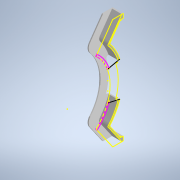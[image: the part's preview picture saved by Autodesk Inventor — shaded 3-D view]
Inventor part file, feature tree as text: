
AUTODESK INVENTOR PART (.ipt)
format: ipt  version: 2022 (Build 260153000, 153)  size: 368,128 bytes
history: native  units: mm
features: reference x28, other x7, projected_geometry x7, sketch x4, extrude x3, fillet x3
ambient origin geometry x8: Origin, YZ Plane, XZ Plane, XY Plane, X Axis, Y Axis, Z Axis, Center Point
bodies: Body1 (feature_tree)
feature tree (52):
  extrude  "Выдавливание5"  Depth=118.0mm
  fillet  "Сопряжение1"  Radius=6.108652mm
  fillet  "Сопряжение2"  Radius=6.108652mm
  sketch  "Эскиз7"
  other  "РабПлоскость1"
  extrude  "Выдавливание6"  Depth=1.5mm
  sketch  "Эскиз9"
  fillet  "Сопряжение3"  Radius=1.5mm
  extrude  "Выдавливание8"  Depth=35.0mm
  sketch  "Эскиз6"
  reference  "Ссылка4"
  reference  "Ссылка5"
  reference  "Ссылка6"
  reference  "Ссылка7"
  reference  "Ссылка8"
  reference  "Ссылка9"
  reference  "Ссылка10"
  reference  "Ссылка11"
  reference  "Ссылка12"
  reference  "Ссылка13"
  reference  "Ссылка14"
  reference  "Ссылка15"
  reference  "Ссылка16"
  reference  "Ссылка17"
  reference  "Ссылка18"
  reference  "Ссылка19"
  reference  "Ссылка20"
  reference  "Ссылка21"
  reference  "Ссылка22"
  reference  "Ссылка23"
  reference  "Ссылка24"
  reference  "Ссылка25"
  reference  "Ссылка26"
  reference  "Ссылка27"
  reference  "Ссылка28"
  reference  "Ссылка29"
  reference  "Ссылка30"
  projected_geometry  "Спроецированная петля4"
  reference  "Ссылка31"
  projected_geometry  "Спроецированная петля8"
  projected_geometry  "Спроецированная петля9"
  projected_geometry  "Спроецированная петля10"
  projected_geometry  "Спроецированная петля11"
  projected_geometry  "Спроецированная петля12"
  sketch  "Эскиз10"
  projected_geometry  "Спроецированная петля13"
  other  "<userpath>\Documents\Git\MZCAT_2024\MZCAT.iam"
  other  "MZCAT.iam"
  other  "vydacha_chertezh:1"
  other  "CAT_protector:1"
  other  "CAT_wheel:3"
  other  "magazine:1"
